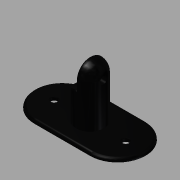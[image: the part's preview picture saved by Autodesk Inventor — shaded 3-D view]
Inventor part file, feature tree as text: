
AUTODESK INVENTOR PART (.ipt)
format: ipt  version: 2014 (Build 180170000, 170)  size: 267,264 bytes
history: native  units: mm
features: fillet x6, sketch x4, extrude x3
ambient origin geometry x8: Origin, YZ Plane, XZ Plane, XY Plane, X Axis, Y Axis, Z Axis, Center Point
bodies: Solid1 (feature_tree)
feature tree (13):
  sketch  "Sketch1"  dims[d0=50.0mm d1=60.0mm d2=12.0mm]
  extrude  "Extrusion6"  Depth=60.0mm
  fillet  "Fillet1"  Radius=12.0mm
  extrude  "Extrusion7"  Depth=10.0mm
  fillet  "Fillet2"  Radius=5.0mm
  fillet  "Fillet3"  Radius=10.0mm
  extrude  "Extrusion9"  Depth=20.0mm
  fillet  "Fillet7"  Radius=20.0mm
  fillet  "Fillet8"  Radius=9.5mm
  fillet  "Fillet9"  Radius=22.0mm
  sketch  "Sketch6"  dims[d3=12.0mm d4=5.0mm d5=5.0mm d20=10.0mm]
  sketch  "Sketch8"  dims[d21=20.0mm d22=5.0mm d23=20.0mm d24=0.0mm d25=9.5mm d27=22.0mm]
  sketch  "Sketch10"  dims[d28=20.0mm d29=0.0mm d30=1.0mm d31=1.0mm d37=80.0mm d38=40.0mm d39=30.0mm d40=4.7mm d41=2.3mm d42=0.0mm d43=0.5mm d44=20.0mm d45=2.0mm]
